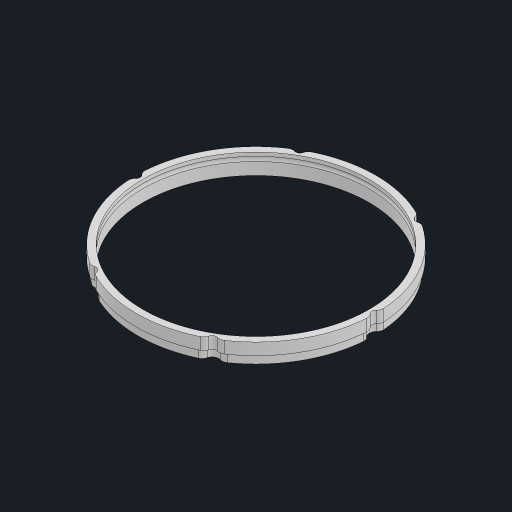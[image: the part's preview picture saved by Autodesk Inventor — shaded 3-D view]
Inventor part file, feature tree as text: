
AUTODESK INVENTOR PART (.ipt)
format: ipt  version: 2023.2 (Build 272271030, 271C)  size: 197,120 bytes
history: native  units: mm
features: sketch x3, extrude x2, revolve x1, fillet x1, pattern_circular x1
ambient origin geometry x8: Origin, YZ Plane, XZ Plane, XY Plane, X Axis, Y Axis, Z Axis, Center Point
bodies: Solid1 (feature_tree)
feature tree (8):
  revolve  "Revolution1"  [1 undecoded]
  extrude  "Extrusion1"  Depth=7.0mm
  extrude  "Extrusion2"  TaperAngle=360.0deg  [1 undecoded]
  fillet  "Fillet1"  Radius=5.1mm
  pattern_circular  "Circular Pattern1"  [2 undecoded]
  sketch  "Sketch1"  dims[d0=5.0mm d1=70.0mm]
  sketch  "Sketch2"  dims[d3=71.0mm d4=7.0mm]
  sketch  "Sketch3"  dims[d7=67.0mm d15=360.0deg d16=5.1mm d17=71.25mm d18=10.0mm d19=0.0mm d20=8.0mm d21=10.0mm d22=0.0mm d23=4.0mm d24=60.0mm d25=360.0deg d27=4.0mm d28=67.5mm]
note: 4 required parameter values undecoded (feature->parameter linkage not recoverable at this tier; creation-order binding heuristic only, values carry confidence <= 0.55)